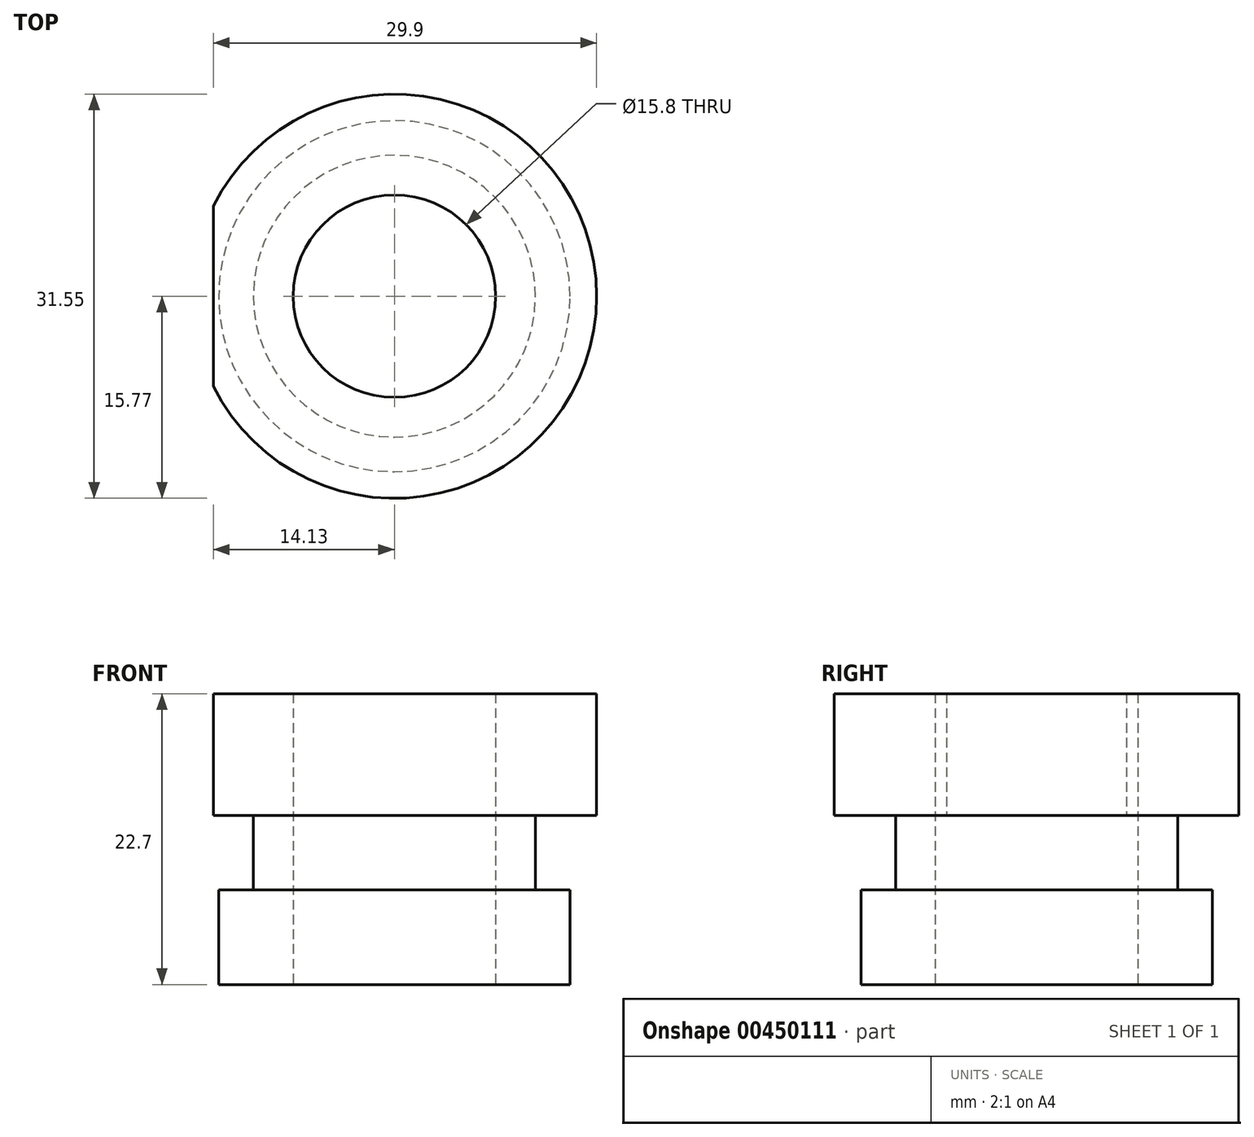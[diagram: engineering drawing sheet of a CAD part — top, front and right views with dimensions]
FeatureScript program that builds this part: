
annotation { "Feature Type Name" : "Feature", "Feature Type Description" : "" }
export const myFeature = defineFeature(function(context is Context, id is Id, definition is map)
    precondition{}
    {
        {
            var Q0;
            Q0=qCreatedBy(makeId("Top.planeOp"),FACE);
            var sketch = newSketch(context, id + "F0", { "sketchPlane" : qUnion([Q0])});
            skArc(sketch, "E0", {"start": v(-14.12, -7.02) * mm, "mid": v(15.78, 0) * mm, "end": v(-14.12, 7.02) * mm});
            skCircle(sketch, "E1", {"center": v(0, 0) * mm, "radius": 7.9 * mm});
            skLineSegment(sketch, "E2", {"start": v(-14.12, 7.02) * mm, "end": v(-14.12, -7.02) * mm});
            skCircle(sketch, "E3", {"center": v(0, 0) * mm, "radius": 11 * mm});
            skSolve(sketch);
        }
        {
            var Q0;
            Q0=makeQuery(id+"F0.imprint","IMPRINT",FACE,{"disambiguationData":[TD([[makeQuery(id+"F0.imprint","IMPRINT",EDGE,{"derivedFrom":sQuery(id+"F0.wireOp",EDGE,"E0")}),1.0]])]});
            var Q1;
            Q1=makeQuery(id+"F0.imprint","IMPRINT",FACE,{"disambiguationData":[TD([[makeQuery(id+"F0.imprint","IMPRINT",EDGE,{"derivedFrom":sQuery(id+"F0.wireOp",EDGE,"E1")}),-1.0]])]});
            var Q2;
            Q2=sQuery(id+"F0.wireOp",EDGE,"E2");
            var Q3;
            Q3=sQuery(id+"F0.wireOp",EDGE,"E0");
            var Q4;
            Q4=sQuery(id+"F0.wireOp",EDGE,"E1");
            extrude(context, id + "F1", {"entities" : qUnion([Q0, Q1]), "surfaceEntities" : qUnion([Q2, Q3, Q4]), "depth" : 9.5 * mm});
        }
        {
            var Q0;
            Q0=makeQuery(id+"F0.imprint","IMPRINT",FACE,{"disambiguationData":[TD([[makeQuery(id+"F0.imprint","IMPRINT",EDGE,{"derivedFrom":sQuery(id+"F0.wireOp",EDGE,"E1")}),-1.0]])]});
            extrude(context, id + "F2", {"entities" : qUnion([Q0]), "operationType" : NewBodyOperationType.ADD, "oppositeDirection" : true, "depth" : 5.8 * mm});
        }
        {
            var Q0;
            Q0=makeQuery(id+"F2.opExtrude","CAP_FACE",FACE,{"disambiguationData":[OSD([sQuery(id+"F0.wireOp",EDGE,"E1"),sQuery(id+"F0.wireOp",EDGE,"E3")])],"isStart":false});
            var sketch = newSketch(context, id + "F3", { "sketchPlane" : qUnion([Q0])});
            skCircle(sketch, "E4", {"center": v(0, 0) * mm, "radius": 13.7 * mm});
            skCircle(sketch, "E5", {"center": v(0, 0) * mm, "radius": 7.9 * mm});
            skSolve(sketch);
        }
        {
            var Q0;
            Q0=makeQuery(id+"F3.imprint","IMPRINT",FACE,{"disambiguationData":[TD([[makeQuery(id+"F3.imprint","IMPRINT",EDGE,{"derivedFrom":sQuery(id+"F3.wireOp",EDGE,"E4")}),1.0]])]});
            var Q1;
            Q1=makeQuery(id+"F3.imprint","IMPRINT",FACE,{"disambiguationData":[TD([[makeQuery(id+"F3.imprint","IMPRINT",EDGE,{"derivedFrom":sQuery(id+"F3.wireOp",EDGE,"E5")}),1.0]])]});
            extrude(context, id + "F4", {"entities" : qUnion([Q0, Q1]), "operationType" : NewBodyOperationType.ADD, "depth" : 7.4 * mm});
        }
    });
